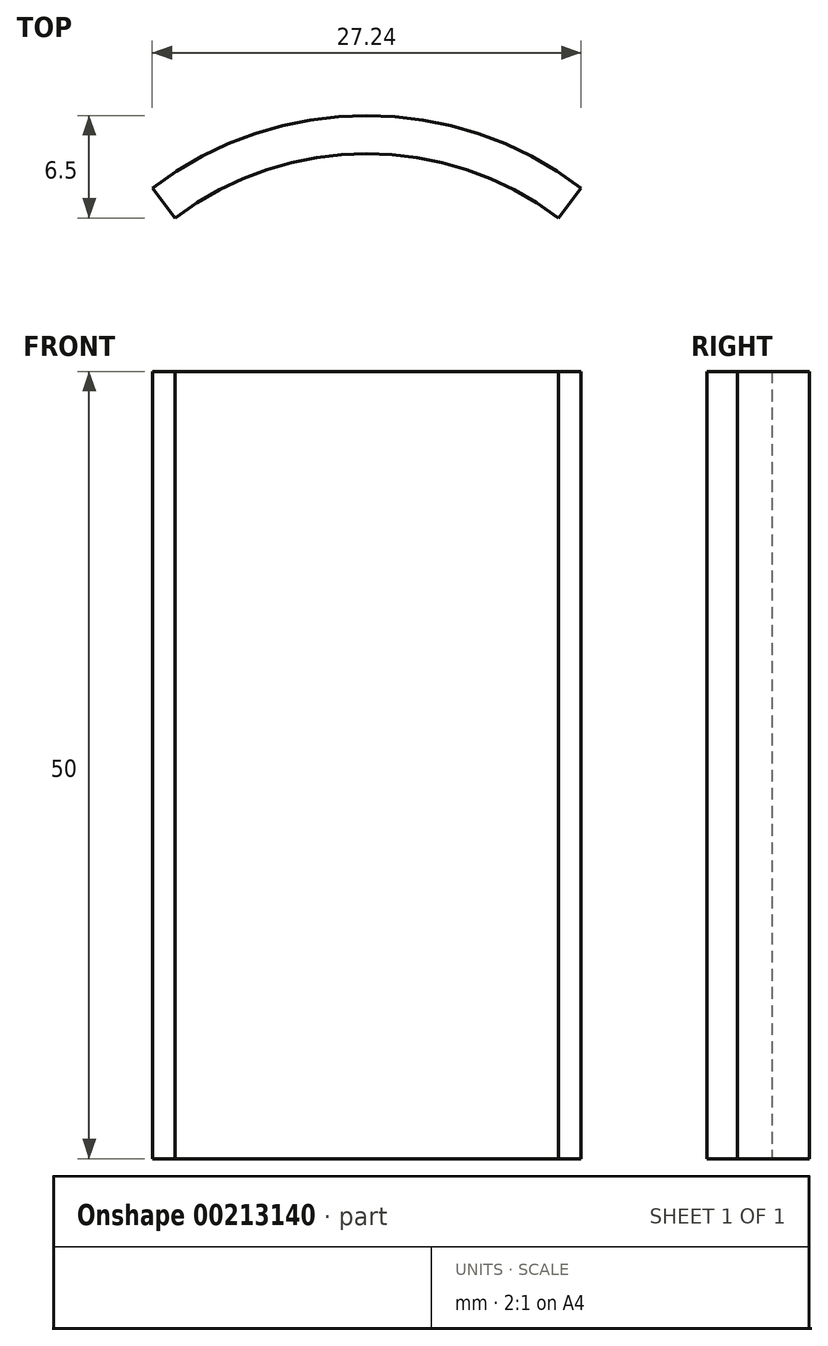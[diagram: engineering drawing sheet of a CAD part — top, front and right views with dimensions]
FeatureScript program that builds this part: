
annotation { "Feature Type Name" : "Feature", "Feature Type Description" : "" }
export const myFeature = defineFeature(function(context is Context, id is Id, definition is map)
    precondition{}
    {
        {
            var Q0;
            Q0=qCreatedBy(makeId("Top.planeOp"),FACE);
            var sketch = newSketch(context, id + "F0", { "sketchPlane" : qUnion([Q0])});
            skArc(sketch, "E0", {"start": v(12.17, 16) * mm, "mid": v(0, 20.1) * mm, "end": v(-12.17, 16) * mm});
            skArc(sketch, "E1", {"start": v(13.62, 17.91) * mm, "mid": v(0, 22.5) * mm, "end": v(-13.62, 17.91) * mm});
            skLineSegment(sketch, "E2", {"start": v(-13.62, 17.91) * mm, "end": v(-12.17, 16) * mm});
            skLineSegment(sketch, "E3", {"start": v(0, 22.5) * mm, "end": v(0, 0) * mm, "construction": true});
            skLineSegment(sketch, "E4.MirrorCS", {"start": v(13.62, 17.91) * mm, "end": v(12.17, 16) * mm});
            skSolve(sketch);
        }
        {
            var Q0;
            Q0 = qSketchRegion(id + "F0", true);
            extrude(context, id + "F1", {"entities" : qUnion([Q0]), "depth" : 50 * mm});
        }
    });
